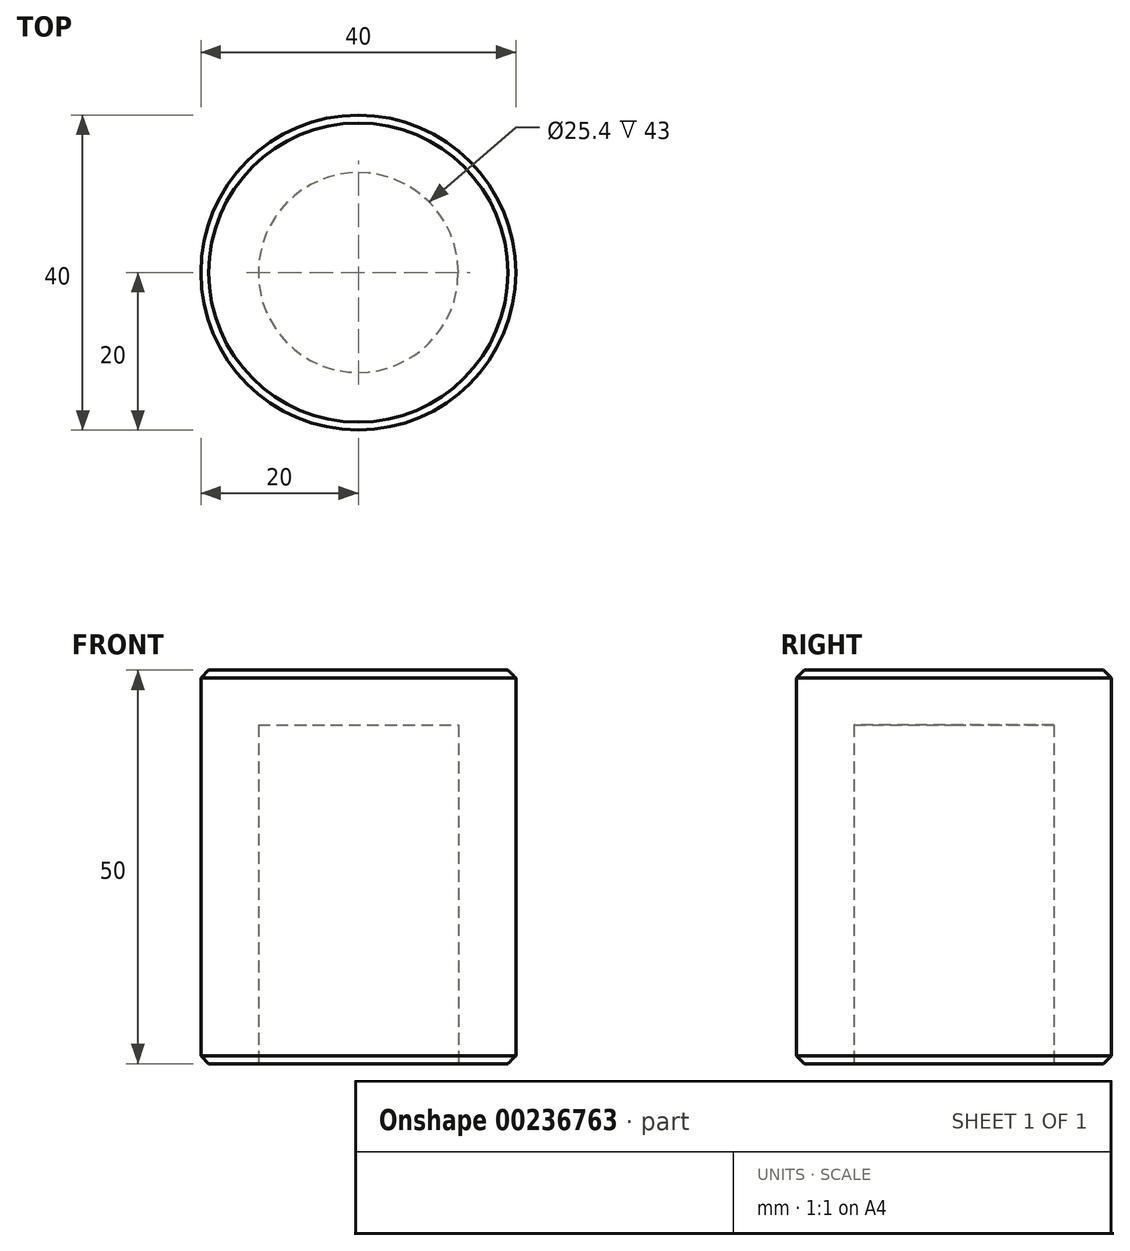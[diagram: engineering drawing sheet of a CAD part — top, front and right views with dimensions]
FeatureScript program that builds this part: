
annotation { "Feature Type Name" : "Feature", "Feature Type Description" : "" }
export const myFeature = defineFeature(function(context is Context, id is Id, definition is map)
    precondition{}
    {
        {
            var Q0;
            Q0=qCreatedBy(makeId("Top.planeOp"),FACE);
            var sketch = newSketch(context, id + "F0", { "sketchPlane" : qUnion([Q0])});
            skCircle(sketch, "E0", {"center": v(0, 0) * mm, "radius": 20 * mm});
            skSolve(sketch);
        }
        {
            var Q0;
            Q0 = qSketchRegion(id + "F0", true);
            extrude(context, id + "F1", {"entities" : qUnion([Q0]), "depth" : 50 * mm, "offsetDistance" : 25 * mm});
        }
        {
            var Q0;
            Q0=makeQuery(id+"F1.opExtrude","CAP_FACE",FACE,{"disambiguationData":[OSD([sQuery(id+"F0.wireOp",EDGE,"E0")])],"isStart":true});
            var sketch = newSketch(context, id + "F2", { "sketchPlane" : qUnion([Q0])});
            skCircle(sketch, "E1", {"center": v(0, 0) * mm, "radius": 12.7 * mm});
            skSolve(sketch);
        }
        {
            var Q0;
            Q0 = qSketchRegion(id + "F2", true);
            extrude(context, id + "F3", {"entities" : qUnion([Q0]), "operationType" : NewBodyOperationType.REMOVE, "oppositeDirection" : true, "depth" : (35 + 8) * mm, "offsetDistance" : 25 * mm});
        }
        {
            var Q0;
            Q0=makeQuery(id+"F3.boolean.opBoolean","COPY",EDGE,{"derivedFrom":makeQuery(id+"F3.opExtrude","CAP_EDGE",EDGE,{"disambiguationData":[OSD([sQuery(id+"F2.wireOp",EDGE,"E1")])],"isStart":true})});
            var Q1;
            Q1=makeQuery(id+"F1.opExtrude","CAP_EDGE",EDGE,{"disambiguationData":[OSD([sQuery(id+"F0.wireOp",EDGE,"E0")])],"isStart":true});
            var Q2;
            Q2=makeQuery(id+"F1.opExtrude","CAP_EDGE",EDGE,{"disambiguationData":[OSD([sQuery(id+"F0.wireOp",EDGE,"E0")])],"isStart":false});
            chamfer(context, id + "F4", {"entities" : qUnion([Q0, Q1, Q2]), "width" : 1 * mm, "tangentPropagation" : true});
        }
    });
